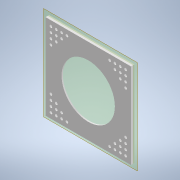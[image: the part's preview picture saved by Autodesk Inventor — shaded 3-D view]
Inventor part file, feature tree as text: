
AUTODESK INVENTOR PART (.ipt)
format: ipt  version: 2020 (Build 240168000, 168)  size: 1,111,040 bytes
history: native  units: in
note: dims shown in document units (in); Inventor stores cm internally (conversion verified against a paired STEP export)
features: extrude x4, sketch x4, plane x1
ambient origin geometry x8: Origin, YZ Plane, XZ Plane, XY Plane, X Axis, Y Axis, Z Axis, Center Point
bodies: Solid1 (feature_tree)
feature tree (9):
  extrude  "Extrusion1"  Depth=0.125in TaperAngle=0.0deg
  plane  "Work Plane1"
  extrude  "Extrusion2"  Depth=0.0845in TaperAngle=0.0deg
  extrude  "Extrusion3"  Depth=5.0in
  extrude  "Extrusion4"  Depth=0.5in
  sketch  "Sketch1"  dims[d0=8.0in d1=0.125in d2=0.0in]
  sketch  "Sketch2"  dims[d3=0.0845in d4=0.25in d5=0.0in]
  sketch  "Sketch3"  dims[d6=0.0039in d7=5.0in]
  sketch  "Sketch4"  dims[d8=0.25in d9=0.0in d10=0.5in d11=0.5in d12=0.25in d13=1.5748in d15=0.5in d16=1.5748in d18=0.5in d21=0.0in d22=0.0in d23=1.5748in d25=360.0deg]
